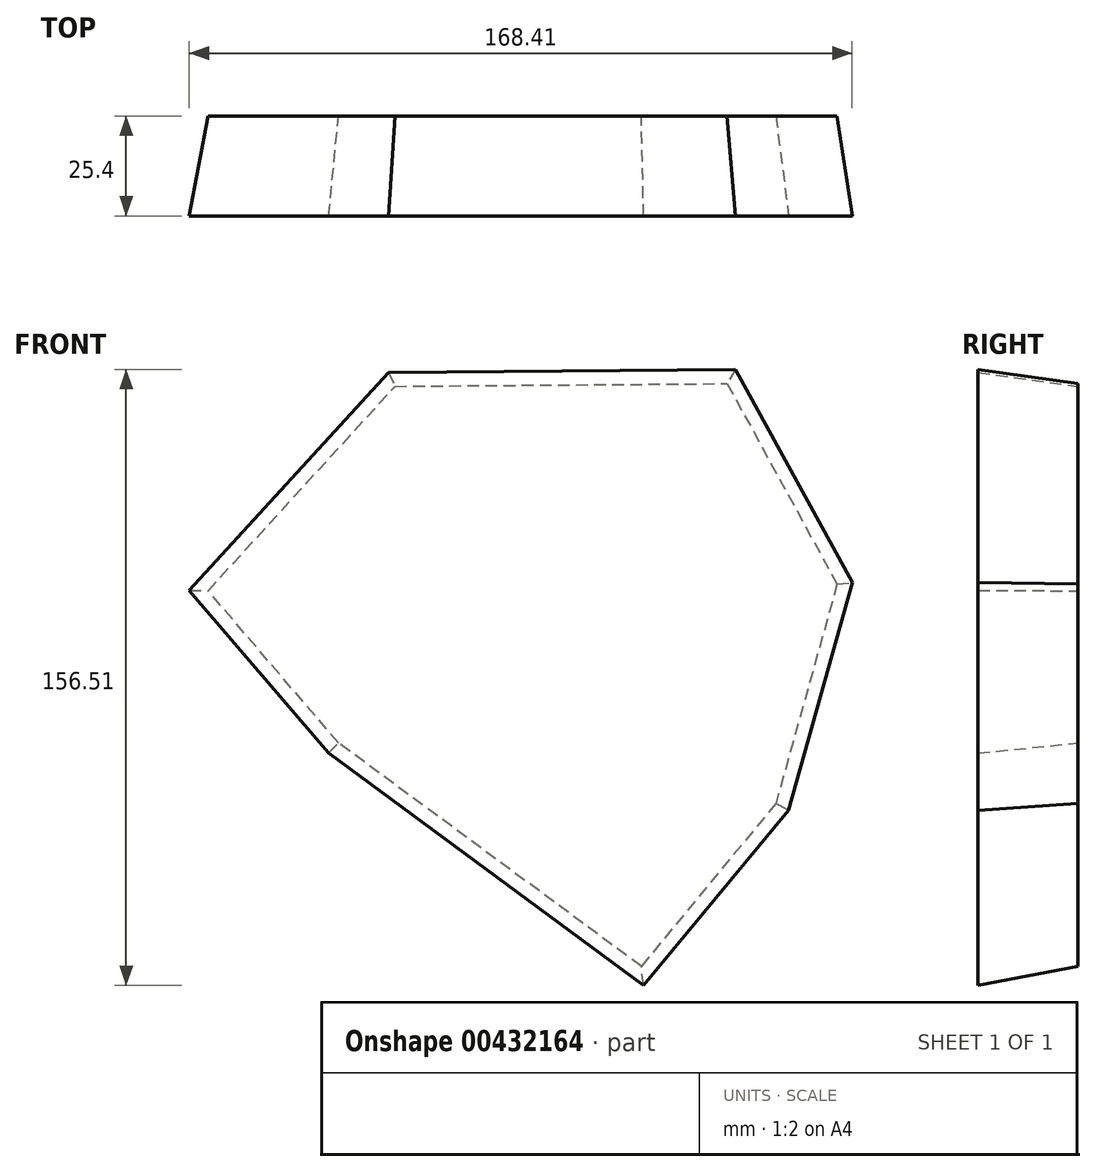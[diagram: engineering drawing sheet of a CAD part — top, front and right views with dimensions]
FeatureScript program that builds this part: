
annotation { "Feature Type Name" : "Feature", "Feature Type Description" : "" }
export const myFeature = defineFeature(function(context is Context, id is Id, definition is map)
    precondition{}
    {
        {
            var Q0;
            Q0=qCreatedBy(makeId("Front.planeOp"),FACE);
            var sketch = newSketch(context, id + "F0", { "sketchPlane" : qUnion([Q0])});
            skLineSegment(sketch, "E0", {"start": v(27.93, 14.43) * mm, "end": v(0, 65.4) * mm});
            skLineSegment(sketch, "E1", {"start": v(0, 65.4) * mm, "end": v(-84.41, 64.72) * mm});
            skLineSegment(sketch, "E2", {"start": v(-84.41, 64.72) * mm, "end": v(-131.88, 12.75) * mm});
            skLineSegment(sketch, "E3", {"start": v(-131.88, 12.75) * mm, "end": v(-98.76, -25.86) * mm});
            skLineSegment(sketch, "E4", {"start": v(-98.76, -25.86) * mm, "end": v(-21.83, -82.65) * mm});
            skLineSegment(sketch, "E5", {"start": v(-21.83, -82.65) * mm, "end": v(12.36, -41.3) * mm});
            skLineSegment(sketch, "E6", {"start": v(27.93, 14.43) * mm, "end": v(12.36, -41.3) * mm});
            skSolve(sketch);
        }
        {
            var Q0;
            Q0=makeQuery(id+"F0.imprint","IMPRINT",FACE,{"disambiguationData":[TD([[makeQuery(id+"F0.imprint","IMPRINT",EDGE,{"derivedFrom":sQuery(id+"F0.wireOp",EDGE,"E0")}),1.0]])]});
            extrude(context, id + "F1", {"entities" : qUnion([Q0]), "depth" : 25.4 * mm, "hasDraft" : true, "draftAngle" : 8 * degree});
        }
    });
